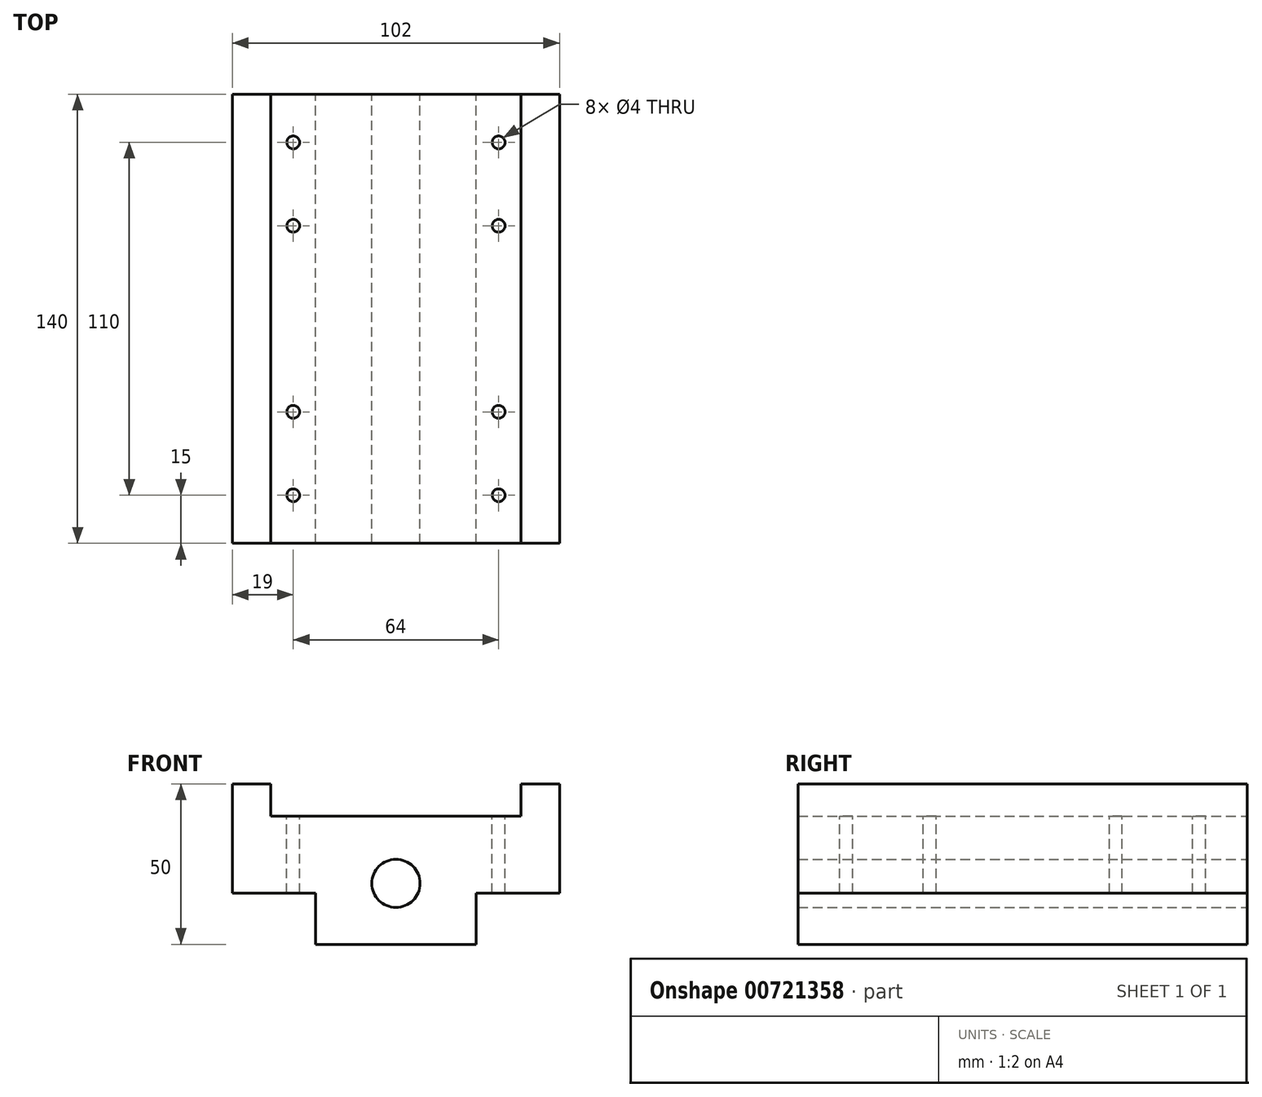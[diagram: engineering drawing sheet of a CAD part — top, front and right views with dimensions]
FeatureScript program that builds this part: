
annotation { "Feature Type Name" : "Feature", "Feature Type Description" : "" }
export const myFeature = defineFeature(function(context is Context, id is Id, definition is map)
    precondition{}
    {
        {
            var Q0;
            Q0=qCreatedBy(makeId("Front.planeOp"),FACE);
            var sketch = newSketch(context, id + "F0", { "sketchPlane" : qUnion([Q0])});
            skLineSegment(sketch, "E0.bottom", {"start": v(51, -17) * mm, "end": v(25, -17) * mm});
            skLineSegment(sketch, "E0.top", {"start": v(51, 17) * mm, "end": v(39, 17) * mm});
            skLineSegment(sketch, "E0.left", {"start": v(51, -17) * mm, "end": v(51, 17) * mm});
            skLineSegment(sketch, "E0.right", {"start": v(-51, -17) * mm, "end": v(-51, 17) * mm});
            skPoint(sketch, "E0.middle", {"position": v(0, 0) * mm});
            skLineSegment(sketch, "E1.top", {"start": v(-39, 7) * mm, "end": v(39, 7) * mm});
            skLineSegment(sketch, "E1.left", {"start": v(-39, 17) * mm, "end": v(-39, 7) * mm});
            skLineSegment(sketch, "E1.right", {"start": v(39, 17) * mm, "end": v(39, 7) * mm});
            skLineSegment(sketch, "E2.trimOffspring", {"start": v(-39, 17) * mm, "end": v(-51, 17) * mm});
            skCircle(sketch, "E3", {"center": v(0, -14) * mm, "radius": 7.5 * mm});
            skLineSegment(sketch, "E4.top", {"start": v(-25, -33) * mm, "end": v(25, -33) * mm});
            skLineSegment(sketch, "E4.left", {"start": v(-25, -17) * mm, "end": v(-25, -33) * mm});
            skLineSegment(sketch, "E4.right", {"start": v(25, -17) * mm, "end": v(25, -33) * mm});
            skLineSegment(sketch, "E5.trimOffspring", {"start": v(-25, -17) * mm, "end": v(-51, -17) * mm});
            skSolve(sketch);
        }
        {
            var Q0;
            Q0=makeQuery(id+"F0.imprint","IMPRINT",FACE,{"disambiguationData":[TD([[makeQuery(id+"F0.imprint","IMPRINT",EDGE,{"derivedFrom":sQuery(id+"F0.wireOp",EDGE,"E0.bottom")}),-1.0]])]});
            extrude(context, id + "F1", {"entities" : qUnion([Q0]), "endBound" : BoundingType.SYMMETRIC, "depth" : 140 * mm, "offsetDistance" : 25 * mm});
        }
        {
            var Q0;
            Q0=makeQuery(id+"F1.opExtrude","SWEPT_FACE",FACE,{"disambiguationData":[OSD([sQuery(id+"F0.wireOp",EDGE,"E1.top")])]});
            var sketch = newSketch(context, id + "F2", { "sketchPlane" : qUnion([Q0])});
            skCircle(sketch, "E6", {"center": v(-32, 55) * mm, "radius": 2 * mm});
            skCircle(sketch, "E7", {"center": v(-32, 29) * mm, "radius": 2 * mm});
            skCircle(sketch, "E8.MirrorC", {"center": v(32, 55) * mm, "radius": 2 * mm});
            skCircle(sketch, "E9.MirrorC", {"center": v(32, 29) * mm, "radius": 2 * mm});
            skCircle(sketch, "E10.MirrorC", {"center": v(-32, -55) * mm, "radius": 2 * mm});
            skCircle(sketch, "E11.MirrorC", {"center": v(32, -29) * mm, "radius": 2 * mm});
            skCircle(sketch, "E12.MirrorC", {"center": v(-32, -29) * mm, "radius": 2 * mm});
            skCircle(sketch, "E13.MirrorC", {"center": v(32, -55) * mm, "radius": 2 * mm});
            skSolve(sketch);
        }
        {
            var Q0;
            Q0 = qSketchRegion(id + "F2", true);
            extrude(context, id + "F3", {"entities" : qUnion([Q0]), "operationType" : NewBodyOperationType.REMOVE, "endBound" : BoundingType.THROUGH_ALL, "oppositeDirection" : true, "depth" : 25 * mm, "offsetDistance" : 25 * mm});
        }
    });
